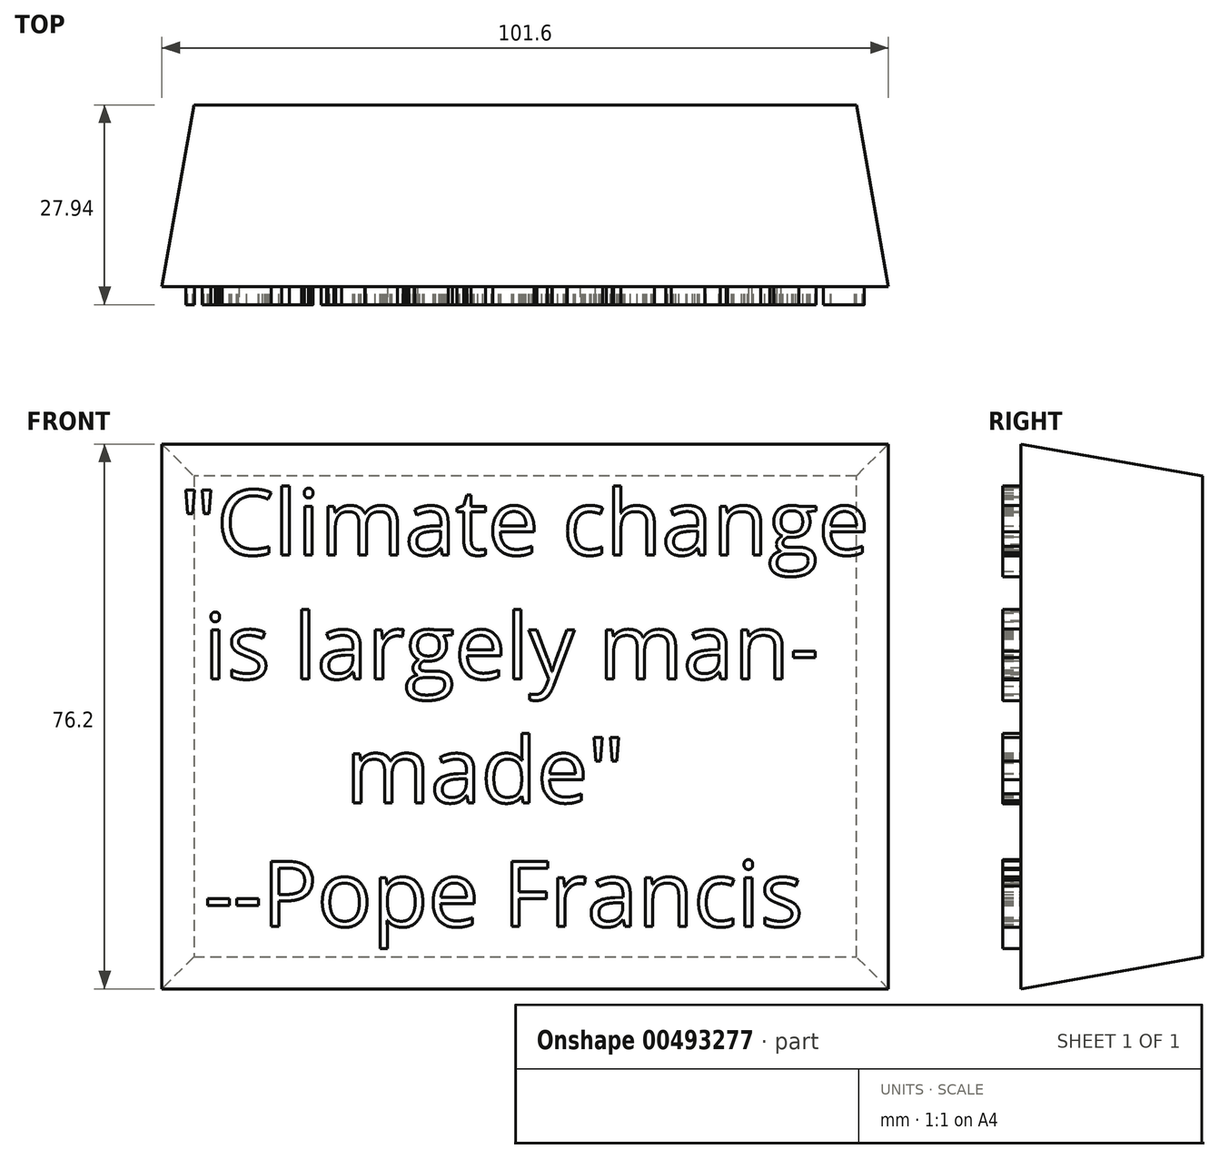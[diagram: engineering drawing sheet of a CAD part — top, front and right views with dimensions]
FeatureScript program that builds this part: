
annotation { "Feature Type Name" : "Feature", "Feature Type Description" : "" }
export const myFeature = defineFeature(function(context is Context, id is Id, definition is map)
    precondition{}
    {
        {
            var Q0;
            Q0=qCreatedBy(makeId("Front.planeOp"),FACE);
            var sketch = newSketch(context, id + "F0", { "sketchPlane" : qUnion([Q0])});
            skLineSegment(sketch, "E0.bottom", {"start": v(-101.6, 76.2) * mm, "end": v(0, 76.2) * mm});
            skLineSegment(sketch, "E0.top", {"start": v(-101.6, 0) * mm, "end": v(0, 0) * mm});
            skLineSegment(sketch, "E0.left", {"start": v(-101.6, 76.2) * mm, "end": v(-101.6, 0) * mm});
            skLineSegment(sketch, "E0.right", {"start": v(0, 76.2) * mm, "end": v(0, 0) * mm});
            skSolve(sketch);
        }
        {
            var Q0;
            Q0=qSketchRegion(id+"F0",true);
            extrude(context, id + "F1", {"entities" : qUnion([Q0]), "oppositeDirection" : true, "depth" : 25.4 * mm, "hasDraft" : true, "draftAngle" : 10 * degree, "draftPullDirection" : true});
        }
        {
            var Q0;
            Q0=makeQuery(id+"F1.opExtrude","CAP_FACE",FACE,{"disambiguationData":[OSD([sQuery(id+"F0.wireOp",EDGE,"E0.bottom"),sQuery(id+"F0.wireOp",EDGE,"E0.top"),sQuery(id+"F0.wireOp",EDGE,"E0.left"),sQuery(id+"F0.wireOp",EDGE,"E0.right")])],"isStart":true});
            var sketch = newSketch(context, id + "F2", { "sketchPlane" : qUnion([Q0])});
            skText(sketch, "E1", { "text": "\"Climate change\n is largely man-\n       made\"\n --Pope Francis", "fontName": "OpenSans-Regular.ttf"});
            const initialGuessF2  = {"E1": [-0.09906, 0.06068, 1, 0, 0.00917]};
            skSetInitialGuess(sketch, initialGuessF2);
            skSolve(sketch);
        }
        {
            var Q0;
            Q0=qSketchRegion(id+"F2",true);
            extrude(context, id + "F3", {"entities" : qUnion([Q0]), "operationType" : NewBodyOperationType.ADD, "depth" : 2.54 * mm});
        }
    });
